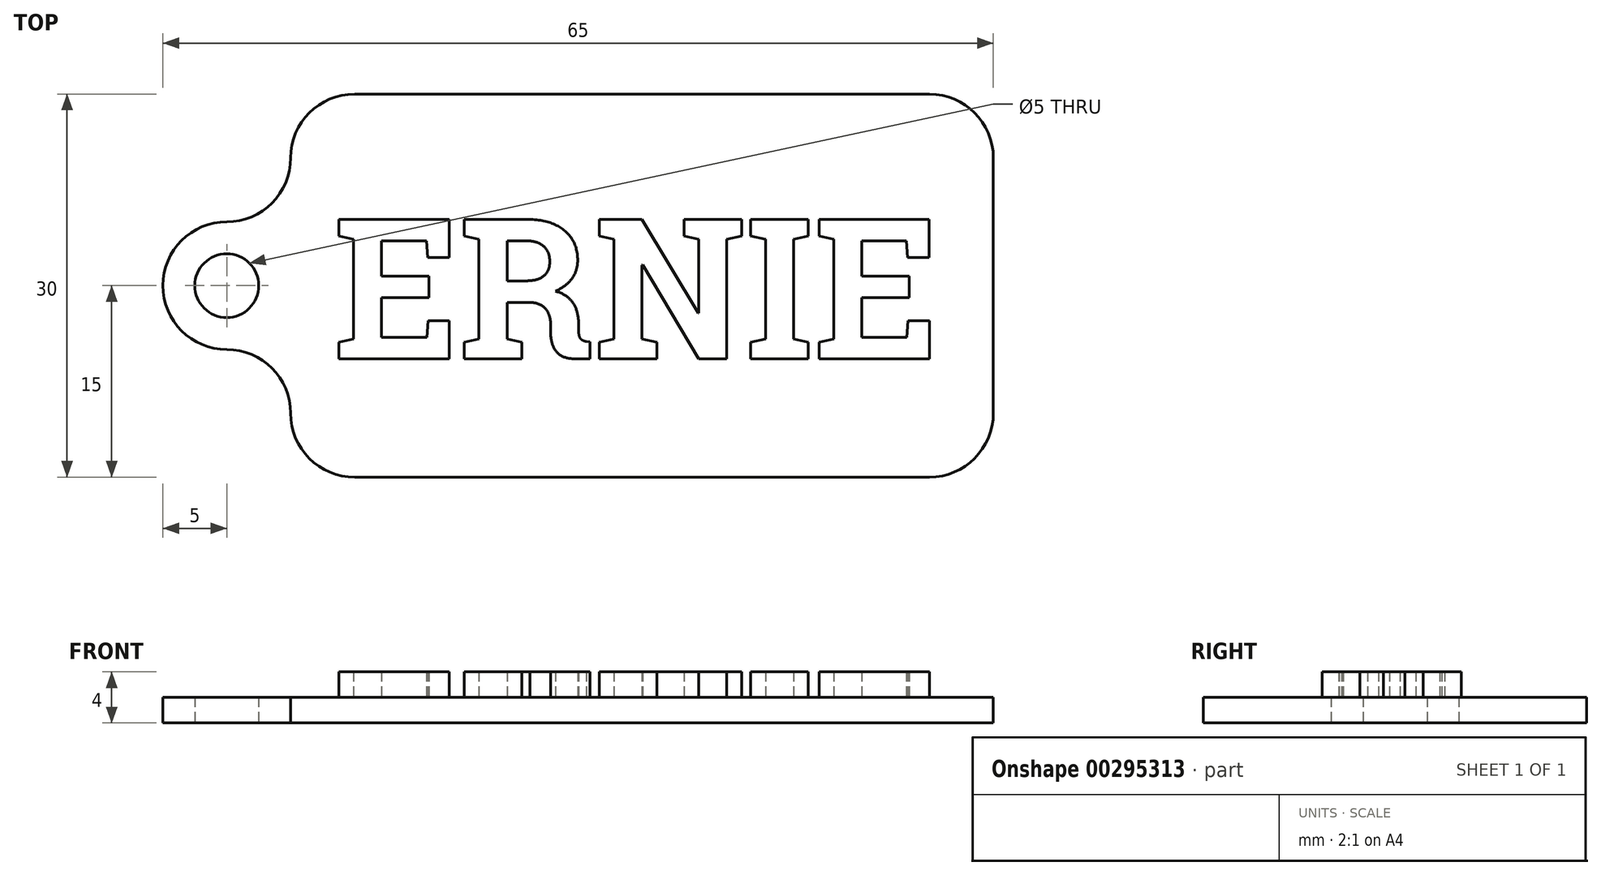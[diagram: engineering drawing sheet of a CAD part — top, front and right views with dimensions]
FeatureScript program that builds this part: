
annotation { "Feature Type Name" : "Feature", "Feature Type Description" : "" }
export const myFeature = defineFeature(function(context is Context, id is Id, definition is map)
    precondition{}
    {
        {
            var Q0;
            Q0=qCreatedBy(makeId("Top.planeOp"),FACE);
            var sketch = newSketch(context, id + "F0", { "sketchPlane" : qUnion([Q0])});
            skLineSegment(sketch, "E0.bottom", {"start": v(22.5, 15) * mm, "end": v(-22.5, 15) * mm});
            skLineSegment(sketch, "E0.top", {"start": v(22.5, -15) * mm, "end": v(-22.5, -15) * mm});
            skLineSegment(sketch, "E0.left", {"start": v(27.5, 10) * mm, "end": v(27.5, -10) * mm});
            skLineSegment(sketch, "E0.right", {"start": v(-27.5, 10) * mm, "end": v(-27.5, 10) * mm});
            skPoint(sketch, "E0.middle", {"position": v(0, 0) * mm});
            skLineSegment(sketch, "E1.bottom", {"start": v(-32.5, 5) * mm, "end": v(-32.5, 5) * mm});
            skLineSegment(sketch, "E1.top", {"start": v(-32.5, -5) * mm, "end": v(-32.5, -5) * mm});
            skLineSegment(sketch, "E1.left", {"start": v(-37.5, 0) * mm, "end": v(-37.5, 0) * mm});
            skLineSegment(sketch, "E2.trimOffspring", {"start": v(-27.5, -10) * mm, "end": v(-27.5, -10) * mm});
            skPoint(sketch, "E3.visualSharp", {"position": v(-37.5, 5) * mm});
            skArc(sketch, "E3.filletArc", {"start": v(-32.5, 5) * mm, "mid": v(-36.04, 3.54) * mm, "end": v(-37.5, 0) * mm});
            skPoint(sketch, "E4.visualSharp", {"position": v(-37.5, -5) * mm});
            skArc(sketch, "E4.filletArc", {"start": v(-37.5, 0) * mm, "mid": v(-36.04, -3.54) * mm, "end": v(-32.5, -5) * mm});
            skPoint(sketch, "E5.visualSharp", {"position": v(-27.5, 15) * mm});
            skArc(sketch, "E5.filletArc", {"start": v(-22.5, 15) * mm, "mid": v(-26.04, 13.54) * mm, "end": v(-27.5, 10) * mm});
            skPoint(sketch, "E6.visualSharp", {"position": v(-27.5, -15) * mm});
            skArc(sketch, "E6.filletArc", {"start": v(-27.5, -10) * mm, "mid": v(-26.04, -13.54) * mm, "end": v(-22.5, -15) * mm});
            skPoint(sketch, "E7.visualSharp", {"position": v(27.5, -15) * mm});
            skArc(sketch, "E7.filletArc", {"start": v(22.5, -15) * mm, "mid": v(26.04, -13.54) * mm, "end": v(27.5, -10) * mm});
            skPoint(sketch, "E8.visualSharp", {"position": v(27.5, 15) * mm});
            skArc(sketch, "E8.filletArc", {"start": v(27.5, 10) * mm, "mid": v(26.04, 13.54) * mm, "end": v(22.5, 15) * mm});
            skCircle(sketch, "E9", {"center": v(-32.5, 0) * mm, "radius": 2.5 * mm});
            skArc(sketch, "E10.filletArc", {"start": v(-32.5, 5) * mm, "mid": v(-28.96, 6.46) * mm, "end": v(-27.5, 10) * mm});
            skArc(sketch, "E11.filletArc", {"start": v(-27.5, -10) * mm, "mid": v(-28.96, -6.46) * mm, "end": v(-32.5, -5) * mm});
            skSolve(sketch);
        }
        {
            var Q0;
            Q0=makeQuery(id+"F0.imprint","IMPRINT",FACE,{"disambiguationData":[TD([[makeQuery(id+"F0.imprint","IMPRINT",EDGE,{"derivedFrom":sQuery(id+"F0.wireOp",EDGE,"E0.bottom")}),1.0]])]});
            extrude(context, id + "F1", {"entities" : qUnion([Q0]), "depth" : 2 * mm});
        }
        {
            var Q0;
            Q0=makeQuery(id+"F1.opExtrude","CAP_FACE",FACE,{"disambiguationData":[OSD([sQuery(id+"F0.wireOp",EDGE,"E0.bottom"),sQuery(id+"F0.wireOp",EDGE,"E0.top"),sQuery(id+"F0.wireOp",EDGE,"E0.left"),sQuery(id+"F0.wireOp",EDGE,"E3.filletArc"),sQuery(id+"F0.wireOp",EDGE,"E4.filletArc"),sQuery(id+"F0.wireOp",EDGE,"E5.filletArc"),sQuery(id+"F0.wireOp",EDGE,"E6.filletArc"),sQuery(id+"F0.wireOp",EDGE,"E7.filletArc"),sQuery(id+"F0.wireOp",EDGE,"E8.filletArc"),sQuery(id+"F0.wireOp",EDGE,"E9"),sQuery(id+"F0.wireOp",EDGE,"E10.filletArc"),sQuery(id+"F0.wireOp",EDGE,"E11.filletArc")])],"isStart":false});
            var sketch = newSketch(context, id + "F2", { "sketchPlane" : qUnion([Q0])});
            skText(sketch, "E12", { "text": "ERNIE", "fontName": "RobotoSlab-Bold.ttf"});
            const initialGuessF2  = {"E12": [-0.02415, -0.00573, 1, 0, 0.01106]};
            skSetInitialGuess(sketch, initialGuessF2);
            skSolve(sketch);
        }
        {
            var Q0;
            Q0=makeQuery(id+"F2.imprint","IMPRINT",FACE,{"disambiguationData":[TD([[makeQuery(id+"F2.imprint","IMPRINT",EDGE,{"derivedFrom":sQuery(id+"F2.wireOp",EDGE,"E12.sketch_text.stroke-0")}),-1.0]])]});
            var Q1;
            Q1=makeQuery(id+"F2.imprint","IMPRINT",FACE,{"disambiguationData":[TD([[makeQuery(id+"F2.imprint","IMPRINT",EDGE,{"derivedFrom":sQuery(id+"F2.wireOp",EDGE,"E12.sketch_text.stroke-12")}),-1.0]])]});
            var Q2;
            Q2=makeQuery(id+"F2.imprint","IMPRINT",FACE,{"disambiguationData":[TD([[makeQuery(id+"F2.imprint","IMPRINT",EDGE,{"derivedFrom":sQuery(id+"F2.wireOp",EDGE,"E12.sketch_text.stroke-31")}),-1.0]])]});
            var Q3;
            Q3=makeQuery(id+"F2.imprint","IMPRINT",FACE,{"disambiguationData":[TD([[makeQuery(id+"F2.imprint","IMPRINT",EDGE,{"derivedFrom":sQuery(id+"F2.wireOp",EDGE,"E12.sketch_text.stroke-45")}),-1.0]])]});
            var Q4;
            Q4=makeQuery(id+"F2.imprint","IMPRINT",FACE,{"disambiguationData":[TD([[makeQuery(id+"F2.imprint","IMPRINT",EDGE,{"derivedFrom":sQuery(id+"F2.wireOp",EDGE,"E12.sketch_text.stroke-49")}),-1.0]])]});
            var Q5;
            Q5=makeQuery(id+"F2.imprint","IMPRINT",FACE,{"disambiguationData":[TD([[makeQuery(id+"F2.imprint","IMPRINT",EDGE,{"derivedFrom":sQuery(id+"F2.wireOp",EDGE,"E12.sketch_text.stroke-57")}),-1.0]])]});
            var Q6;
            Q6=makeQuery(id+"F2.imprint","IMPRINT",FACE,{"disambiguationData":[TD([[makeQuery(id+"F2.imprint","IMPRINT",EDGE,{"derivedFrom":sQuery(id+"F2.wireOp",EDGE,"E12.sketch_text.stroke-81")}),-1.0]])]});
            var Q7;
            Q7=makeQuery(id+"F2.imprint","IMPRINT",FACE,{"disambiguationData":[TD([[makeQuery(id+"F2.imprint","IMPRINT",EDGE,{"derivedFrom":sQuery(id+"F2.wireOp",EDGE,"E12.sketch_text.stroke-93")}),-1.0]])]});
            extrude(context, id + "F3", {"entities" : qUnion([Q0, Q1, Q2, Q3, Q4, Q5, Q6, Q7]), "operationType" : NewBodyOperationType.ADD, "depth" : 2 * mm});
        }
    });
